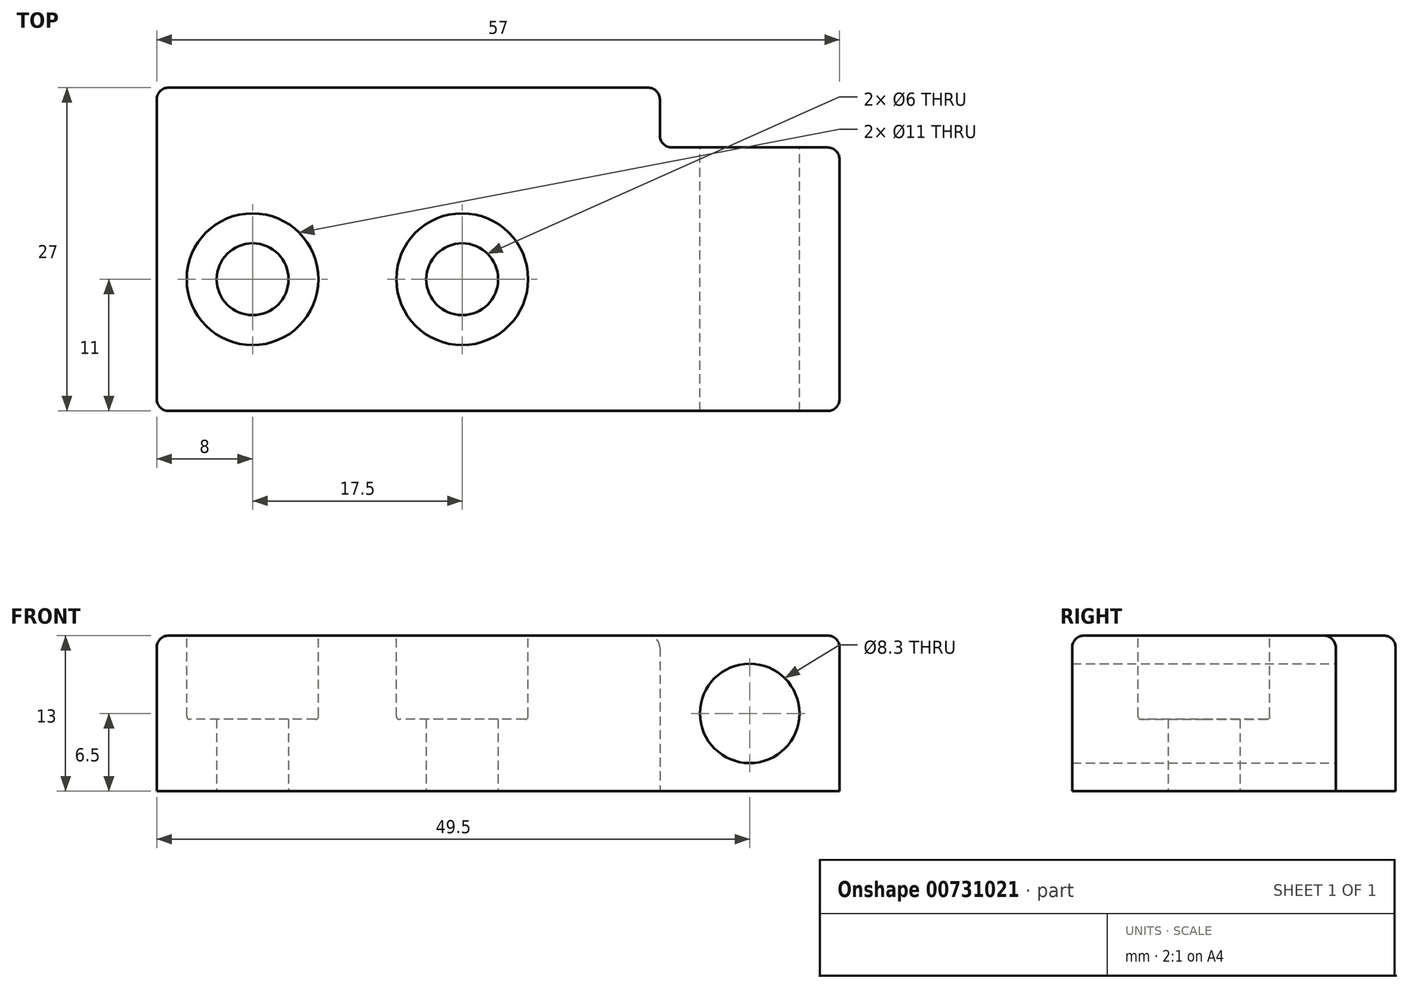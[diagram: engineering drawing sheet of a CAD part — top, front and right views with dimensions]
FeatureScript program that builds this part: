
annotation { "Feature Type Name" : "Feature", "Feature Type Description" : "" }
export const myFeature = defineFeature(function(context is Context, id is Id, definition is map)
    precondition{}
    {
        {
            var Q0;
            Q0=qCreatedBy(makeId("Top.planeOp"),FACE);
            var sketch = newSketch(context, id + "F0", { "sketchPlane" : qUnion([Q0])});
            skLineSegment(sketch, "E0.bottom", {"start": v(-28.5, -13.5) * mm, "end": v(28.5, -13.5) * mm});
            skLineSegment(sketch, "E0.top", {"start": v(-28.5, 13.5) * mm, "end": v(13.5, 13.5) * mm});
            skLineSegment(sketch, "E0.left", {"start": v(-28.5, -13.5) * mm, "end": v(-28.5, 13.5) * mm});
            skLineSegment(sketch, "E0.right", {"start": v(28.5, -13.5) * mm, "end": v(28.5, 8.5) * mm});
            skPoint(sketch, "E0.middle", {"position": v(0, 0) * mm});
            skCircle(sketch, "E1", {"center": v(-20.5, -2.5) * mm, "radius": 3 * mm});
            skCircle(sketch, "E2", {"center": v(-3, -2.5) * mm, "radius": 3 * mm});
            skLineSegment(sketch, "E3.top", {"start": v(28.5, 8.5) * mm, "end": v(13.5, 8.5) * mm});
            skLineSegment(sketch, "E3.right", {"start": v(13.5, 13.5) * mm, "end": v(13.5, 8.5) * mm});
            skPoint(sketch, "E4.orphan", {"position": v(28.5, 13.5) * mm});
            skSolve(sketch);
        }
        {
            var Q0;
            Q0 = qSketchRegion(id + "F0", true);
            extrude(context, id + "F1", {"entities" : qUnion([Q0]), "depth" : 13 * mm, "offsetDistance" : 25 * mm});
        }
        {
            var Q0;
            Q0=makeQuery(id+"F1.opExtrude","SWEPT_FACE",FACE,{"disambiguationData":[OSD([sQuery(id+"F0.wireOp",EDGE,"E3.top")])]});
            var sketch = newSketch(context, id + "F2", { "sketchPlane" : qUnion([Q0])});
            skCircle(sketch, "E5", {"center": v(-21, 6.5) * mm, "radius": 4.15 * mm});
            skPoint(sketch, "E5.centerSnap0", {"position": v(-21, 13) * mm});
            skPoint(sketch, "E5.centerSnap1", {"position": v(-28.5, 6.5) * mm});
            skSolve(sketch);
        }
        {
            var Q0;
            Q0 = qSketchRegion(id + "F2", true);
            extrude(context, id + "F3", {"entities" : qUnion([Q0]), "operationType" : NewBodyOperationType.REMOVE, "endBound" : BoundingType.THROUGH_ALL, "oppositeDirection" : true, "depth" : 25 * mm, "offsetDistance" : 25 * mm});
        }
        {
            var Q0;
            Q0=makeQuery(id+"F1.opExtrude","CAP_FACE",FACE,{"disambiguationData":[OSD([sQuery(id+"F0.wireOp",EDGE,"E0.bottom"),sQuery(id+"F0.wireOp",EDGE,"E0.top"),sQuery(id+"F0.wireOp",EDGE,"E0.left"),sQuery(id+"F0.wireOp",EDGE,"E0.right"),sQuery(id+"F0.wireOp",EDGE,"E1"),sQuery(id+"F0.wireOp",EDGE,"E2"),sQuery(id+"F0.wireOp",EDGE,"E3.top"),sQuery(id+"F0.wireOp",EDGE,"E3.right")])],"isStart":false});
            var sketch = newSketch(context, id + "F4", { "sketchPlane" : qUnion([Q0])});
            skCircle(sketch, "E6", {"center": v(-20.5, -2.5) * mm, "radius": 5.5 * mm});
            skCircle(sketch, "E7", {"center": v(-3, -2.5) * mm, "radius": 5.5 * mm});
            skSolve(sketch);
        }
        {
            var Q0;
            Q0 = qSketchRegion(id + "F4", true);
            extrude(context, id + "F5", {"entities" : qUnion([Q0]), "operationType" : NewBodyOperationType.REMOVE, "oppositeDirection" : true, "depth" : 7 * mm, "offsetDistance" : 25 * mm});
        }
        {
            var Q0;
            Q0=makeQuery(id+"F1.opExtrude","CAP_EDGE",EDGE,{"disambiguationData":[OSD([sQuery(id+"F0.wireOp",EDGE,"E0.bottom")])],"isStart":false});
            var Q1;
            Q1=makeQuery(id+"F1.opExtrude","CAP_EDGE",EDGE,{"disambiguationData":[OSD([sQuery(id+"F0.wireOp",EDGE,"E0.right")])],"isStart":false});
            var Q2;
            Q2=makeQuery(id+"F1.opExtrude","CAP_EDGE",EDGE,{"disambiguationData":[OSD([sQuery(id+"F0.wireOp",EDGE,"E0.top")])],"isStart":false});
            var Q3;
            Q3=makeQuery(id+"F1.opExtrude","CAP_EDGE",EDGE,{"disambiguationData":[OSD([sQuery(id+"F0.wireOp",EDGE,"E3.top")])],"isStart":false});
            var Q4;
            Q4=makeQuery(id+"F1.opExtrude","CAP_EDGE",EDGE,{"disambiguationData":[OSD([sQuery(id+"F0.wireOp",EDGE,"E3.right")])],"isStart":false});
            var Q5;
            Q5=makeQuery(id+"F1.opExtrude","CAP_EDGE",EDGE,{"disambiguationData":[OSD([sQuery(id+"F0.wireOp",EDGE,"E0.left")])],"isStart":false});
            var Q6;
            Q6=makeQuery(id+"F1.opExtrude","SWEPT_EDGE",EDGE,{"disambiguationData":[OSD([sQuery(id+"F0.wireOp",EDGE,"E0.bottom"),sQuery(id+"F0.wireOp",EDGE,"E0.left")])]});
            var Q7;
            Q7=makeQuery(id+"F1.opExtrude","SWEPT_EDGE",EDGE,{"disambiguationData":[OSD([sQuery(id+"F0.wireOp",EDGE,"E0.bottom"),sQuery(id+"F0.wireOp",EDGE,"E0.right")])]});
            var Q8;
            Q8=makeQuery(id+"F1.opExtrude","SWEPT_EDGE",EDGE,{"disambiguationData":[OSD([sQuery(id+"F0.wireOp",EDGE,"E0.right"),sQuery(id+"F0.wireOp",EDGE,"E3.top")])]});
            var Q9;
            Q9=makeQuery(id+"F1.opExtrude","SWEPT_EDGE",EDGE,{"disambiguationData":[OSD([sQuery(id+"F0.wireOp",EDGE,"E3.top"),sQuery(id+"F0.wireOp",EDGE,"E3.right")])]});
            var Q10;
            Q10=makeQuery(id+"F1.opExtrude","SWEPT_EDGE",EDGE,{"disambiguationData":[OSD([sQuery(id+"F0.wireOp",EDGE,"E0.top"),sQuery(id+"F0.wireOp",EDGE,"E3.right")])]});
            var Q11;
            Q11=makeQuery(id+"F1.opExtrude","SWEPT_EDGE",EDGE,{"disambiguationData":[OSD([sQuery(id+"F0.wireOp",EDGE,"E0.top"),sQuery(id+"F0.wireOp",EDGE,"E0.left")])]});
            var Q12;
            Q12=makeQuery(id+"F3.boolean.opBoolean","COPY",EDGE,{"derivedFrom":makeQuery(id+"F3.opExtrude","CAP_EDGE",EDGE,{"disambiguationData":[OSD([sQuery(id+"F2.wireOp",EDGE,"E5")])],"isStart":true})});
            var Q13;
            Q13=makeQuery(id+"F5.boolean.opBoolean","COPY",EDGE,{"derivedFrom":makeQuery(id+"F5.opExtrude","CAP_EDGE",EDGE,{"disambiguationData":[OSD([sQuery(id+"F4.wireOp",EDGE,"E7")])],"isStart":true})});
            var Q14;
            Q14=makeQuery(id+"F5.boolean.opBoolean","COPY",EDGE,{"derivedFrom":makeQuery(id+"F5.opExtrude","CAP_EDGE",EDGE,{"disambiguationData":[OSD([sQuery(id+"F4.wireOp",EDGE,"E6")])],"isStart":true})});
            fillet(context, id + "F6", {"entities" : qUnion([Q0, Q1, Q2, Q3, Q4, Q5, Q6, Q7, Q8, Q9, Q10, Q11, Q12, Q13, Q14]), "radius" : 1 * mm, "tangentPropagation" : true, "allowEdgeOverflow" : false});
        }
        {
            var Q0;
            Q0=makeQuery(id+"F5.boolean.opBoolean","COPY",EDGE,{"derivedFrom":makeQuery(id+"F5.opExtrude","CAP_EDGE",EDGE,{"disambiguationData":[OSD([sQuery(id+"F4.wireOp",EDGE,"E7")])],"isStart":false})});
            var Q1;
            Q1=makeQuery(id+"F5.boolean.opBoolean","COPY",EDGE,{"derivedFrom":makeQuery(id+"F5.opExtrude","CAP_EDGE",EDGE,{"disambiguationData":[OSD([sQuery(id+"F4.wireOp",EDGE,"E6")])],"isStart":false})});
            fillet(context, id + "F7", {"entities" : qUnion([Q0, Q1]), "radius" : .25 * mm, "tangentPropagation" : true, "allowEdgeOverflow" : false});
        }
    });
